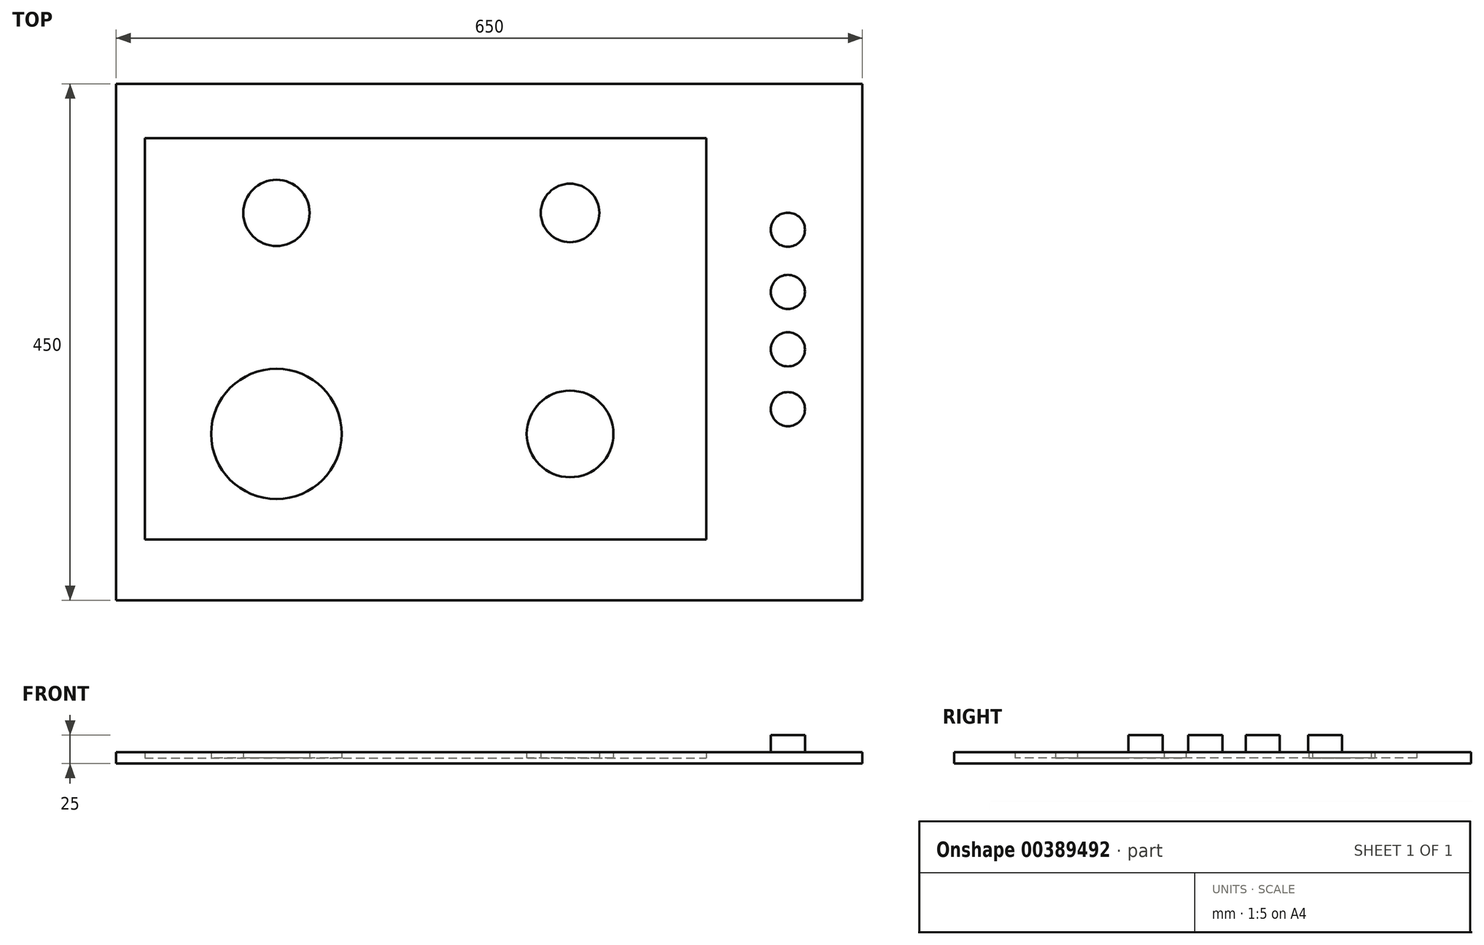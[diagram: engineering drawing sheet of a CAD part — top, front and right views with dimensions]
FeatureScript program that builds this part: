
annotation { "Feature Type Name" : "Feature", "Feature Type Description" : "" }
export const myFeature = defineFeature(function(context is Context, id is Id, definition is map)
    precondition{}
    {
        {
            var Q0;
            Q0=qCreatedBy(makeId("Top.planeOp"),FACE);
            var sketch = newSketch(context, id + "F0", { "sketchPlane" : qUnion([Q0])});
            skLineSegment(sketch, "E0.bottom", {"start": v(-288.21, 93.22) * mm, "end": v(361.79, 93.22) * mm});
            skLineSegment(sketch, "E0.top", {"start": v(-288.21, -356.78) * mm, "end": v(361.79, -356.78) * mm});
            skLineSegment(sketch, "E0.left", {"start": v(-288.21, 93.22) * mm, "end": v(-288.21, -356.78) * mm});
            skLineSegment(sketch, "E0.right", {"start": v(361.79, 93.22) * mm, "end": v(361.79, -356.78) * mm});
            skLineSegment(sketch, "E1.bottom", {"start": v(-263.28, 45.86) * mm, "end": v(225.72, 45.86) * mm});
            skLineSegment(sketch, "E1.top", {"start": v(-263.28, -303.8) * mm, "end": v(225.72, -303.8) * mm});
            skLineSegment(sketch, "E1.left", {"start": v(-263.28, 45.86) * mm, "end": v(-263.28, -303.8) * mm});
            skLineSegment(sketch, "E1.right", {"start": v(225.72, 45.86) * mm, "end": v(225.72, -303.8) * mm});
            skCircle(sketch, "E2", {"center": v(-148.6, -19.2) * mm, "radius": 28.85 * mm});
            skCircle(sketch, "E3", {"center": v(107.14, -19.2) * mm, "radius": 25.5 * mm});
            skCircle(sketch, "E4", {"center": v(107.14, -211.85) * mm, "radius": 37.77 * mm});
            skCircle(sketch, "E5", {"center": v(-148.6, -211.85) * mm, "radius": 56.83 * mm});
            skCircle(sketch, "E6", {"center": v(296.83, -33.83) * mm, "radius": 14.87 * mm});
            skCircle(sketch, "E7", {"center": v(296.83, -88.09) * mm, "radius": 14.87 * mm});
            skCircle(sketch, "E8", {"center": v(296.83, -138.12) * mm, "radius": 14.87 * mm});
            skCircle(sketch, "E9", {"center": v(296.83, -190.27) * mm, "radius": 14.87 * mm});
            skSolve(sketch);
        }
        {
            var Q0;
            Q0=makeQuery(id+"F0.imprint","IMPRINT",FACE,{"disambiguationData":[TD([[makeQuery(id+"F0.imprint","IMPRINT",EDGE,{"derivedFrom":sQuery(id+"F0.wireOp",EDGE,"E0.bottom")}),-1.0]])]});
            extrude(context, id + "F1", {"entities" : qUnion([Q0]), "depth" : 10 * mm});
        }
        {
            var Q0;
            Q0=makeQuery(id+"F0.imprint","IMPRINT",FACE,{"disambiguationData":[TD([[makeQuery(id+"F0.imprint","IMPRINT",EDGE,{"derivedFrom":sQuery(id+"F0.wireOp",EDGE,"E1.bottom")}),-1.0]])]});
            extrude(context, id + "F2", {"entities" : qUnion([Q0]), "operationType" : NewBodyOperationType.ADD, "depth" : 5 * mm});
        }
        {
            var Q0;
            Q0=makeQuery(id+"F0.imprint","IMPRINT",FACE,{"disambiguationData":[TD([[makeQuery(id+"F0.imprint","IMPRINT",EDGE,{"derivedFrom":sQuery(id+"F0.wireOp",EDGE,"E2")}),1.0]])]});
            var Q1;
            Q1=makeQuery(id+"F0.imprint","IMPRINT",FACE,{"disambiguationData":[TD([[makeQuery(id+"F0.imprint","IMPRINT",EDGE,{"derivedFrom":sQuery(id+"F0.wireOp",EDGE,"E3")}),1.0]])]});
            var Q2;
            Q2=makeQuery(id+"F0.imprint","IMPRINT",FACE,{"disambiguationData":[TD([[makeQuery(id+"F0.imprint","IMPRINT",EDGE,{"derivedFrom":sQuery(id+"F0.wireOp",EDGE,"E4")}),1.0]])]});
            var Q3;
            Q3=makeQuery(id+"F0.imprint","IMPRINT",FACE,{"disambiguationData":[TD([[makeQuery(id+"F0.imprint","IMPRINT",EDGE,{"derivedFrom":sQuery(id+"F0.wireOp",EDGE,"E5")}),1.0]])]});
            extrude(context, id + "F3", {"entities" : qUnion([Q0, Q1, Q2, Q3]), "operationType" : NewBodyOperationType.ADD, "depth" : 10 * mm});
        }
        {
            var Q0;
            Q0=makeQuery(id+"F0.imprint","IMPRINT",FACE,{"disambiguationData":[TD([[makeQuery(id+"F0.imprint","IMPRINT",EDGE,{"derivedFrom":sQuery(id+"F0.wireOp",EDGE,"E6")}),1.0]])]});
            var Q1;
            Q1=makeQuery(id+"F0.imprint","IMPRINT",FACE,{"disambiguationData":[TD([[makeQuery(id+"F0.imprint","IMPRINT",EDGE,{"derivedFrom":sQuery(id+"F0.wireOp",EDGE,"E7")}),1.0]])]});
            var Q2;
            Q2=makeQuery(id+"F0.imprint","IMPRINT",FACE,{"disambiguationData":[TD([[makeQuery(id+"F0.imprint","IMPRINT",EDGE,{"derivedFrom":sQuery(id+"F0.wireOp",EDGE,"E8")}),1.0]])]});
            var Q3;
            Q3=makeQuery(id+"F0.imprint","IMPRINT",FACE,{"disambiguationData":[TD([[makeQuery(id+"F0.imprint","IMPRINT",EDGE,{"derivedFrom":sQuery(id+"F0.wireOp",EDGE,"E9")}),1.0]])]});
            extrude(context, id + "F4", {"entities" : qUnion([Q0, Q1, Q2, Q3]), "operationType" : NewBodyOperationType.ADD, "depth" : 25 * mm});
        }
    });
